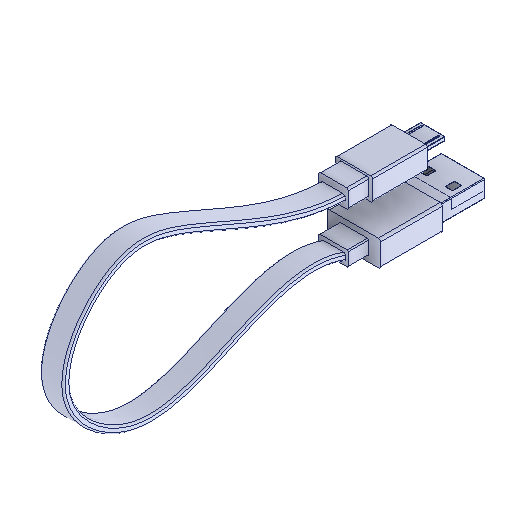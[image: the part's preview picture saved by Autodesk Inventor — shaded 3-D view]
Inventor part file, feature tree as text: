
AUTODESK INVENTOR PART (.ipt)
format: ipt  version: 2024.1 (Build 281209000, 209)  size: 299,008 bytes
history: native  units: mm
features: other x4, sweep x1
ambient origin geometry x8: Origin, YZ Plane, XZ Plane, XY Plane, X Axis, Y Axis, Z Axis, Center Point
bodies: Volumenkörper1 (feature_tree), Volumenkörper2 (feature_tree), Volumenkörper3 (feature_tree), Volumenkörper4 (feature_tree), Volumenkörper5 (feature_tree)
feature tree (5):
  other  "Cut-Extrude1"
  other  "Cut-Extrude2"
  other  "Cut-Extrude3"
  other  "Boss-Extrude8"
  sweep  "Sweep1"
